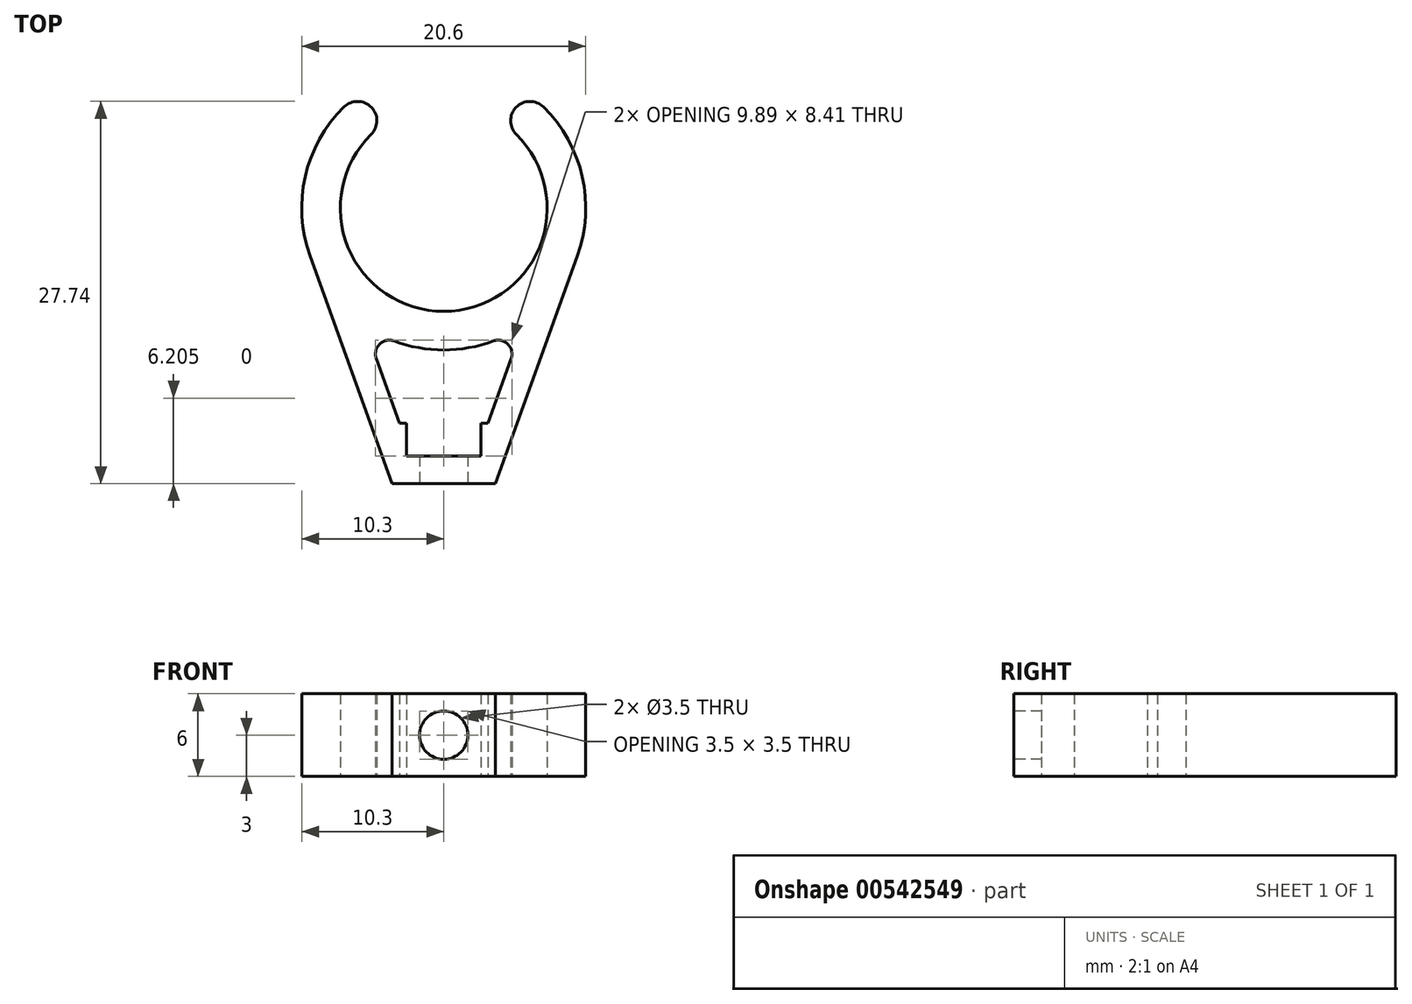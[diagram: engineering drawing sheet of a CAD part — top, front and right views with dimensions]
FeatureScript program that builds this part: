
annotation { "Feature Type Name" : "Feature", "Feature Type Description" : "" }
export const myFeature = defineFeature(function(context is Context, id is Id, definition is map)
    precondition{}
    {
        {
            var Q0;
            Q0=qCreatedBy(makeId("Top.planeOp"),FACE);
            var sketch = newSketch(context, id + "F0", { "sketchPlane" : qUnion([Q0])});
            skArc(sketch, "E0", {"start": v(-5.27, 5.34) * mm, "mid": v(0, -7.5) * mm, "end": v(5.27, 5.34) * mm});
            skLineSegment(sketch, "E1", {"start": v(-3.75, -20) * mm, "end": v(3.75, -20) * mm});
            skArc(sketch, "E2", {"start": v(-3.6, -9.65) * mm, "mid": v(0, -10.3) * mm, "end": v(3.6, -9.65) * mm});
            skLineSegment(sketch, "E3", {"start": v(3.75, -20) * mm, "end": v(9.7, -3.49) * mm});
            skLineSegment(sketch, "E4.MirrorCS", {"start": v(-3.75, -20) * mm, "end": v(-9.7, -3.49) * mm});
            skLineSegment(sketch, "E5.0", {"start": v(3.2, -15.6) * mm, "end": v(4.89, -10.93) * mm});
            skLineSegment(sketch, "E5.1", {"start": v(-2.34, -18) * mm, "end": v(2.34, -18) * mm});
            skLineSegment(sketch, "E5.2", {"start": v(-3.2, -15.6) * mm, "end": v(-4.89, -10.93) * mm});
            skArc(sketch, "E6.trimOffspring", {"start": v(9.7, -3.49) * mm, "mid": v(10.04, 2.28) * mm, "end": v(7.23, 7.33) * mm});
            skLineSegment(sketch, "E7.bottom", {"start": v(-2.7, -18) * mm, "end": v(2.7, -18) * mm});
            skLineSegment(sketch, "E7.top", {"start": v(-3.2, -15.6) * mm, "end": v(-2.7, -15.6) * mm});
            skLineSegment(sketch, "E7.left", {"start": v(-2.7, -18) * mm, "end": v(-2.7, -15.6) * mm});
            skLineSegment(sketch, "E7.right", {"start": v(2.7, -18) * mm, "end": v(2.7, -15.6) * mm});
            skLineSegment(sketch, "E8.trimOffspring", {"start": v(2.7, -15.6) * mm, "end": v(3.2, -15.6) * mm});
            skPoint(sketch, "E9.visualSharp", {"position": v(-5.74, -8.55) * mm});
            skArc(sketch, "E9.filletArc", {"start": v(-3.6, -9.65) * mm, "mid": v(-4.65, -9.88) * mm, "end": v(-4.89, -10.93) * mm});
            skArc(sketch, "E10.MirrorCS", {"start": v(3.6, -9.65) * mm, "mid": v(4.65, -9.88) * mm, "end": v(4.89, -10.93) * mm});
            skArc(sketch, "E11", {"start": v(-5.27, 5.34) * mm, "mid": v(-5.25, 7.32) * mm, "end": v(-7.23, 7.33) * mm});
            skArc(sketch, "E12.MirrorCS", {"start": v(5.27, 5.34) * mm, "mid": v(5.25, 7.32) * mm, "end": v(7.23, 7.33) * mm});
            skArc(sketch, "E13.trimOffspring", {"start": v(-7.23, 7.33) * mm, "mid": v(-10.04, 2.28) * mm, "end": v(-9.7, -3.49) * mm});
            skSolve(sketch);
        }
        {
            var Q0;
            Q0 = qSketchRegion(id + "F0", true);
            extrude(context, id + "F1", {"entities" : qUnion([Q0]), "depth" : 6 * mm, "offsetDistance" : 25 * mm});
        }
        {
            var Q0;
            Q0=makeQuery(id+"F1.opExtrude","SWEPT_FACE",FACE,{"disambiguationData":[OSD([sQuery(id+"F0.wireOp",EDGE,"E1")])]});
            var sketch = newSketch(context, id + "F2", { "sketchPlane" : qUnion([Q0])});
            skLineSegment(sketch, "E14", {"start": v(3.75, 0) * mm, "end": v(-3.75, 6) * mm, "construction": true});
            skCircle(sketch, "E15", {"center": v(0, 3) * mm, "radius": 1.75 * mm});
            skSolve(sketch);
        }
        {
            var Q0;
            Q0=makeQuery(id+"F2.imprint","IMPRINT",FACE,{"disambiguationData":[TD([[makeQuery(id+"F2.imprint","IMPRINT",EDGE,{"derivedFrom":sQuery(id+"F2.wireOp",EDGE,"E15")}),1.0]])]});
            extrude(context, id + "F3", {"entities" : qUnion([Q0]), "operationType" : NewBodyOperationType.REMOVE, "endBound" : BoundingType.UP_TO_NEXT, "oppositeDirection" : true, "depth" : 25 * mm, "offsetDistance" : 25 * mm});
        }
    });
